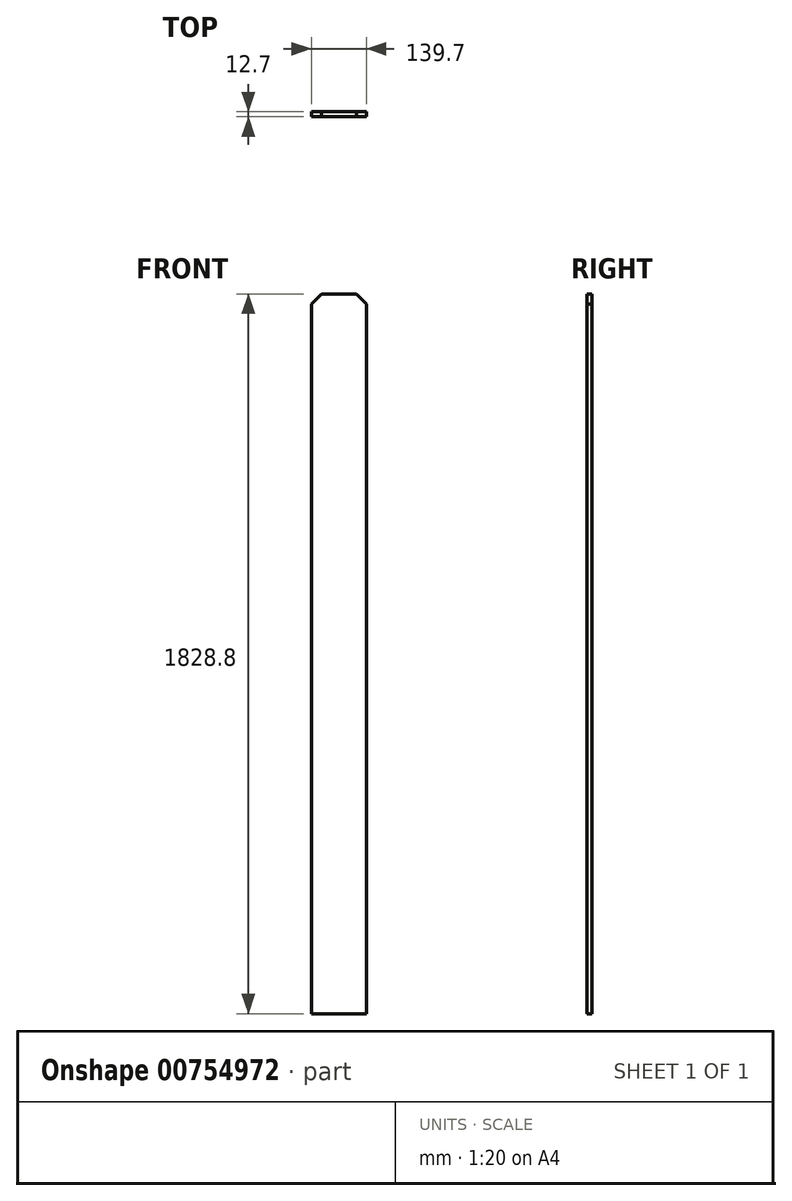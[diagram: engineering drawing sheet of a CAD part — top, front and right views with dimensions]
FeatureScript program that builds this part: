
annotation { "Feature Type Name" : "Feature", "Feature Type Description" : "" }
export const myFeature = defineFeature(function(context is Context, id is Id, definition is map)
    precondition{}
    {
        {
            var Q0;
            Q0=qCreatedBy(makeId("Top.planeOp"),FACE);
            var sketch = newSketch(context, id + "F0", { "sketchPlane" : qUnion([Q0])});
            skLineSegment(sketch, "E0.bottom", {"start": v(0, 0) * mm, "end": v(139.7, 0) * mm});
            skLineSegment(sketch, "E0.top", {"start": v(0, 12.7) * mm, "end": v(139.7, 12.7) * mm});
            skLineSegment(sketch, "E0.left", {"start": v(0, 0) * mm, "end": v(0, 12.7) * mm});
            skLineSegment(sketch, "E0.right", {"start": v(139.7, 0) * mm, "end": v(139.7, 12.7) * mm});
            skSolve(sketch);
        }
        {
            var Q0;
            Q0=makeQuery(id+"F0.imprint","IMPRINT",FACE,{"disambiguationData":[TD([[makeQuery(id+"F0.imprint","IMPRINT",EDGE,{"derivedFrom":sQuery(id+"F0.wireOp",EDGE,"E0.bottom")}),1.0]])]});
            extrude(context, id + "F1", {"entities" : qUnion([Q0]), "depth" : 1828.8 * mm, "offsetDistance" : 25.4 * mm});
        }
        {
            var Q0;
            Q0=makeQuery(id+"F1.opExtrude","CAP_EDGE",EDGE,{"disambiguationData":[OSD([sQuery(id+"F0.wireOp",EDGE,"E0.right")])],"isStart":false});
            var Q1;
            Q1=makeQuery(id+"F1.opExtrude","CAP_EDGE",EDGE,{"disambiguationData":[OSD([sQuery(id+"F0.wireOp",EDGE,"E0.left")])],"isStart":false});
            chamfer(context, id + "F2", {"entities" : qUnion([Q0, Q1]), "width" : 25.4 * mm, "tangentPropagation" : true});
        }
    });
